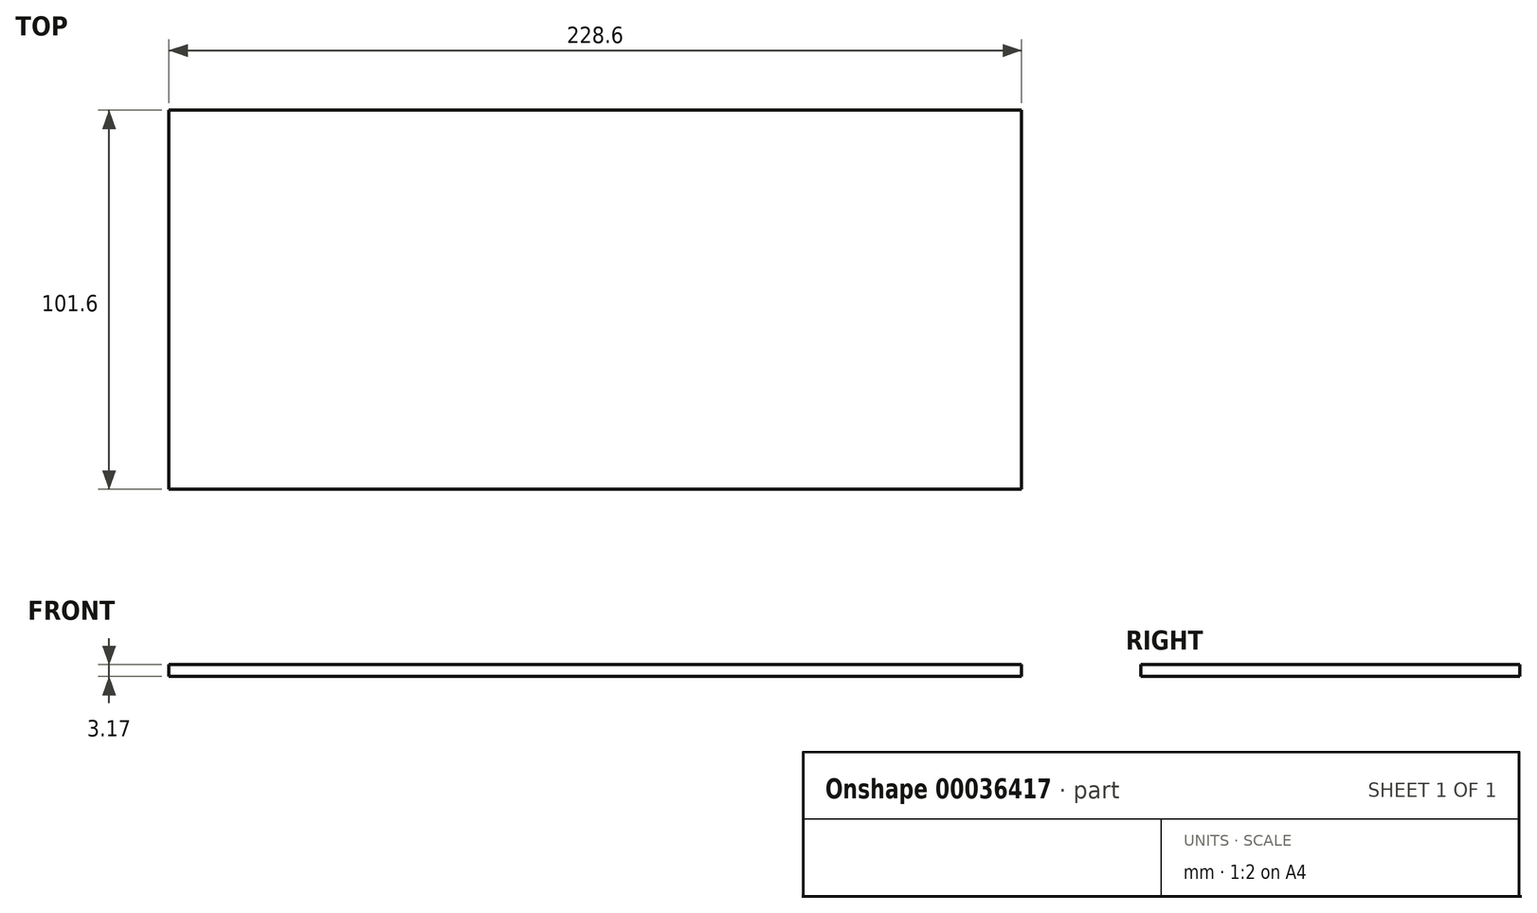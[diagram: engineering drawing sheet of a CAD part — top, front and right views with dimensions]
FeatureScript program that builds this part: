
annotation { "Feature Type Name" : "Feature", "Feature Type Description" : "" }
export const myFeature = defineFeature(function(context is Context, id is Id, definition is map)
    precondition{}
    {
        {
            var Q0;
            Q0=qCreatedBy(makeId("Top.planeOp"),FACE);
            var sketch = newSketch(context, id + "F0", { "sketchPlane" : qUnion([Q0])});
            skLineSegment(sketch, "E0.rect.bottom", {"start": v(114.3, -50.8) * mm, "end": v(-114.3, -50.8) * mm});
            skLineSegment(sketch, "E0.rect.top", {"start": v(114.3, 50.8) * mm, "end": v(-114.3, 50.8) * mm});
            skLineSegment(sketch, "E0.rect.left", {"start": v(114.3, -50.8) * mm, "end": v(114.3, 50.8) * mm});
            skLineSegment(sketch, "E0.rect.right", {"start": v(-114.3, -50.8) * mm, "end": v(-114.3, 50.8) * mm});
            skPoint(sketch, "E0.rect.middle", {"position": v(0, 0) * mm});
            skSolve(sketch);
        }
        {
            var Q0;
            Q0=makeQuery(id+"F0.imprint","IMPRINT",FACE,{"disambiguationData":[TD([[makeQuery(id+"F0.imprint","IMPRINT",EDGE,{"derivedFrom":sQuery(id+"F0.wireOp",EDGE,"E0.rect.bottom")}),-1.0]])]});
            extrude(context, id + "F1", {"entities" : qUnion([Q0]), "depth" : 3.17 * mm});
        }
    });
